# Revit family: Урна для раздельного сбора мусора «Урба» Арт 13967
name_source: partatom
category: Антураж
revit_build: Autodesk Revit 2018 (Build: 20180423_1000(x64)
units: mm (PartAtom-declared; Revit-internal decimal feet)

## family parameters
Всегда вертикально = Да
Источник визуального образа = Геометрия семейства
На основе рабочей плоскости = Нет
Общий = Нет
При загрузке вырезать с полостями = Нет
Точка расчета площади = Нет

## types (2) — shared parameters
URL = https://hobbyka.ru
Артикул товара = Арт. 13967
Высота = 1000 мм
Группа модели = Уличные урны
Длина = 500 мм
Изготовитель = ООО «Хоббика»
Материал изделия = Сталь
Цвет бака = Черный
Цвет оконтовки = Хром
Цвет отходов = Синий
Ширина = 400 мм

## per-type parameters (varying)
| type | Без наклейкии | Изображение типоразмера | Наклейка |
| Урна для раздельного сбора мусора «Урба». 1 секция с наклейкой | Нет | Урна для раздельного сбора мусора «Урба» с наклейкой Арт 13967.jpg | Да |
| Урна для раздельного сбора мусора «Урба». 1 секция без наклейки | Да | Урна для раздельного сбора мусора «Урба» без наклейки Арт 13967.jpg | Нет |

note: column(s) folded — value = type name in every type: Описание
